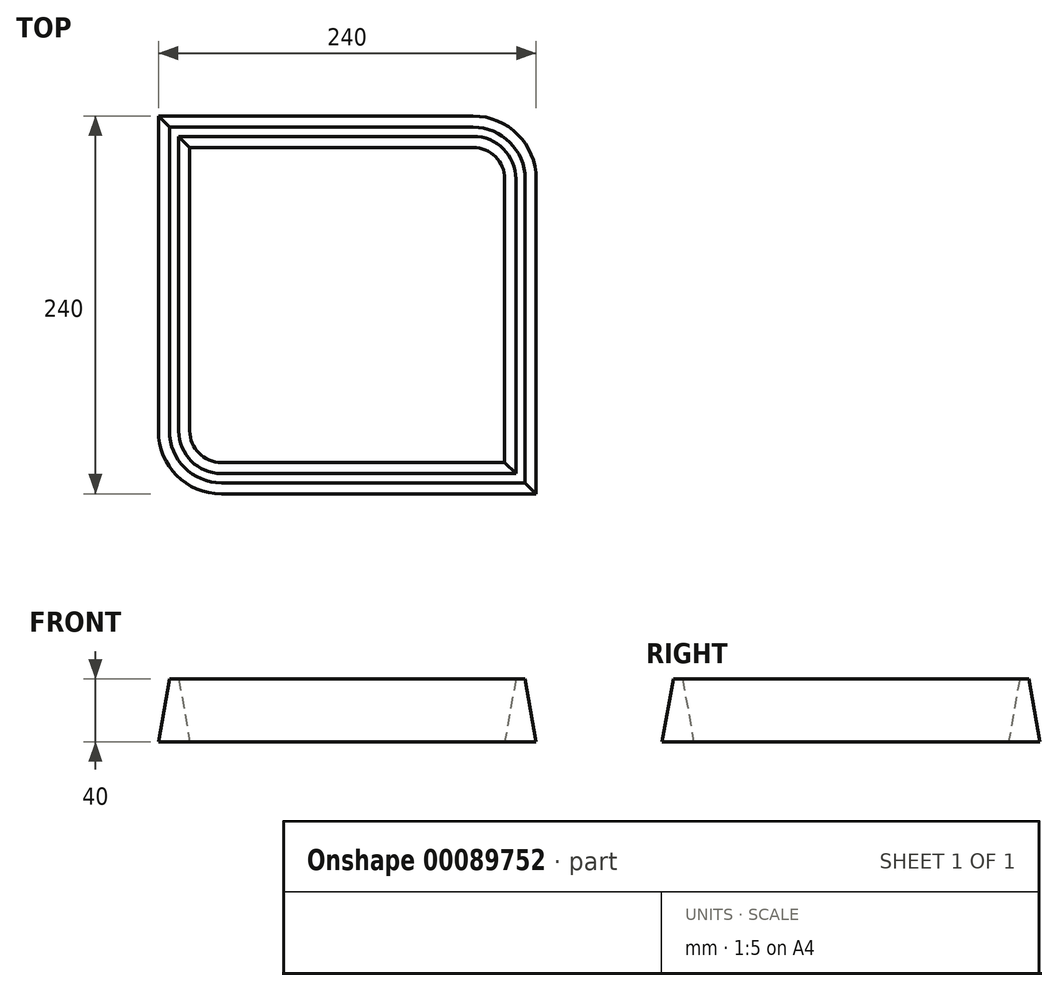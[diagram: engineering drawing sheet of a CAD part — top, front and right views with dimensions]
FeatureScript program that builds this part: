
annotation { "Feature Type Name" : "Feature", "Feature Type Description" : "" }
export const myFeature = defineFeature(function(context is Context, id is Id, definition is map)
    precondition{}
    {
        {
            var Q0;
            Q0=qCreatedBy(makeId("Top.planeOp"),FACE);
            var sketch = newSketch(context, id + "F0", { "sketchPlane" : qUnion([Q0])});
            skLineSegment(sketch, "E0.bottom", {"start": v(80, 100) * mm, "end": v(-100, 100) * mm});
            skLineSegment(sketch, "E0.top", {"start": v(100, -100) * mm, "end": v(-80, -100) * mm});
            skLineSegment(sketch, "E0.left", {"start": v(100, 80) * mm, "end": v(100, -100) * mm});
            skLineSegment(sketch, "E0.right", {"start": v(-100, 100) * mm, "end": v(-100, -80) * mm});
            skPoint(sketch, "E0.middle", {"position": v(0, 0) * mm});
            skPoint(sketch, "E1.visualSharp", {"position": v(100, 100) * mm});
            skArc(sketch, "E1.filletArc", {"start": v(100, 80) * mm, "mid": v(94.14, 94.14) * mm, "end": v(80, 100) * mm});
            skPoint(sketch, "E2.visualSharp", {"position": v(-100, -100) * mm});
            skArc(sketch, "E2.filletArc", {"start": v(-100, -80) * mm, "mid": v(-94.14, -94.14) * mm, "end": v(-80, -100) * mm});
            skLineSegment(sketch, "E3.0", {"start": v(-120, 120) * mm, "end": v(-120, -80) * mm});
            skLineSegment(sketch, "E3.1", {"start": v(120, -120) * mm, "end": v(-80, -120) * mm});
            skLineSegment(sketch, "E3.2", {"start": v(120, 80) * mm, "end": v(120, -120) * mm});
            skArc(sketch, "E3.3", {"start": v(-120, -80) * mm, "mid": v(-108.28, -108.28) * mm, "end": v(-80, -120) * mm});
            skArc(sketch, "E3.4", {"start": v(120, 80) * mm, "mid": v(108.28, 108.28) * mm, "end": v(80, 120) * mm});
            skLineSegment(sketch, "E3.5", {"start": v(80, 120) * mm, "end": v(-120, 120) * mm});
            skSolve(sketch);
        }
        {
            var Q0;
            Q0 = qSketchRegion(id + "F0", true);
            var Q1;
            Q1=makeQuery(id+"F0.imprint","IMPRINT",FACE,{"disambiguationData":[TD([[makeQuery(id+"F0.imprint","IMPRINT",EDGE,{"derivedFrom":sQuery(id+"F0.wireOp",EDGE,"E0.bottom")}),-1.0]])]});
            extrude(context, id + "F1", {"entities" : qUnion([Q0, Q1]), "depth" : 40 * mm, "hasDraft" : true, "draftAngle" : 10 * degree, "draftPullDirection" : true});
        }
    });
